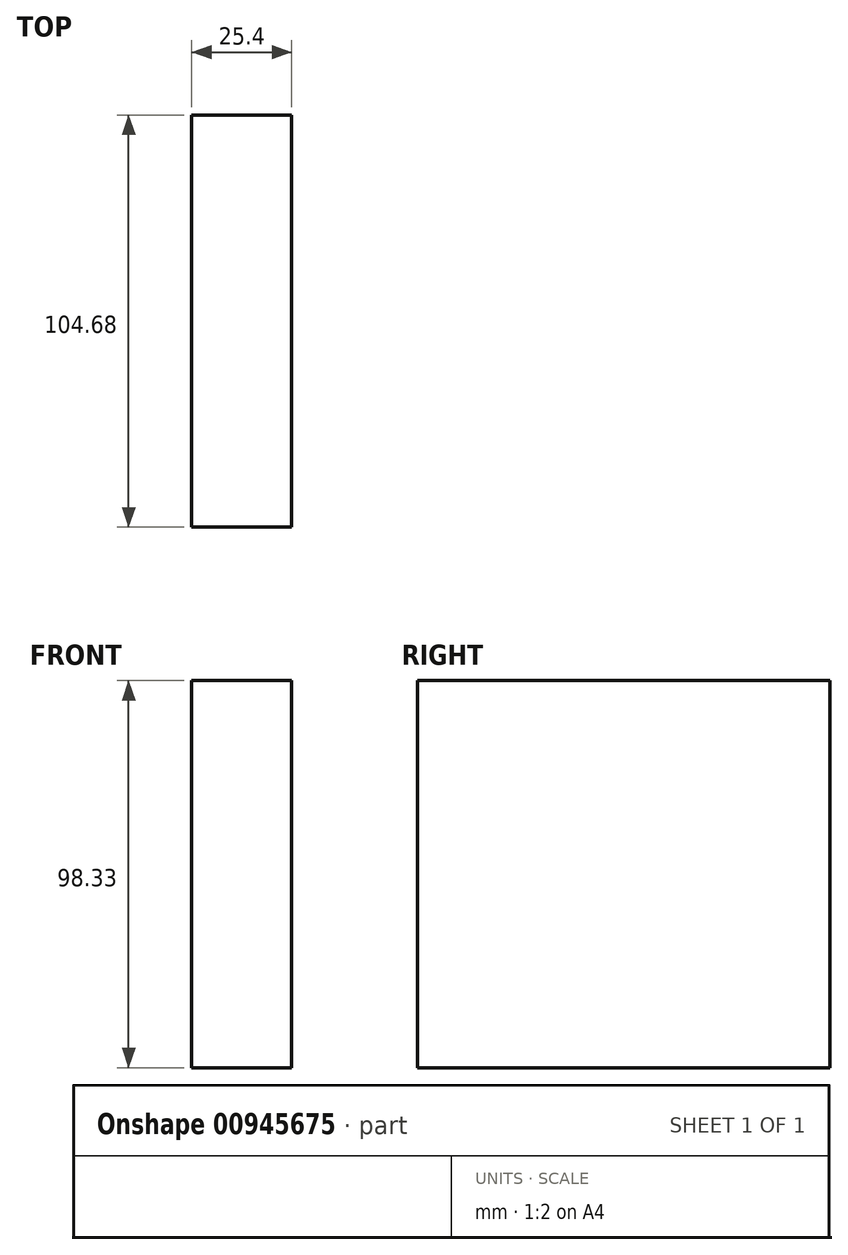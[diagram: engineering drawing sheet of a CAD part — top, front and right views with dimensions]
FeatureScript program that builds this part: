
annotation { "Feature Type Name" : "Feature", "Feature Type Description" : "" }
export const myFeature = defineFeature(function(context is Context, id is Id, definition is map)
    precondition{}
    {
        {
            var Q0;
            Q0=qCreatedBy(makeId("Right.planeOp"),FACE);
            var sketch = newSketch(context, id + "F0", { "sketchPlane" : qUnion([Q0])});
            skLineSegment(sketch, "E0.bottom", {"start": v(53.67, -53.7) * mm, "end": v(-51, -53.7) * mm});
            skLineSegment(sketch, "E0.top", {"start": v(53.67, 44.64) * mm, "end": v(-51, 44.64) * mm});
            skLineSegment(sketch, "E0.left", {"start": v(53.67, -53.7) * mm, "end": v(53.67, 44.64) * mm});
            skLineSegment(sketch, "E0.right", {"start": v(-51, -53.7) * mm, "end": v(-51, 44.64) * mm});
            skSolve(sketch);
        }
        {
            var Q0;
            Q0 = qSketchRegion(id + "F0", true);
            extrude(context, id + "F1", {"entities" : qUnion([Q0]), "depth" : 25.4 * mm, "offsetDistance" : 25.4 * mm});
        }
    });
